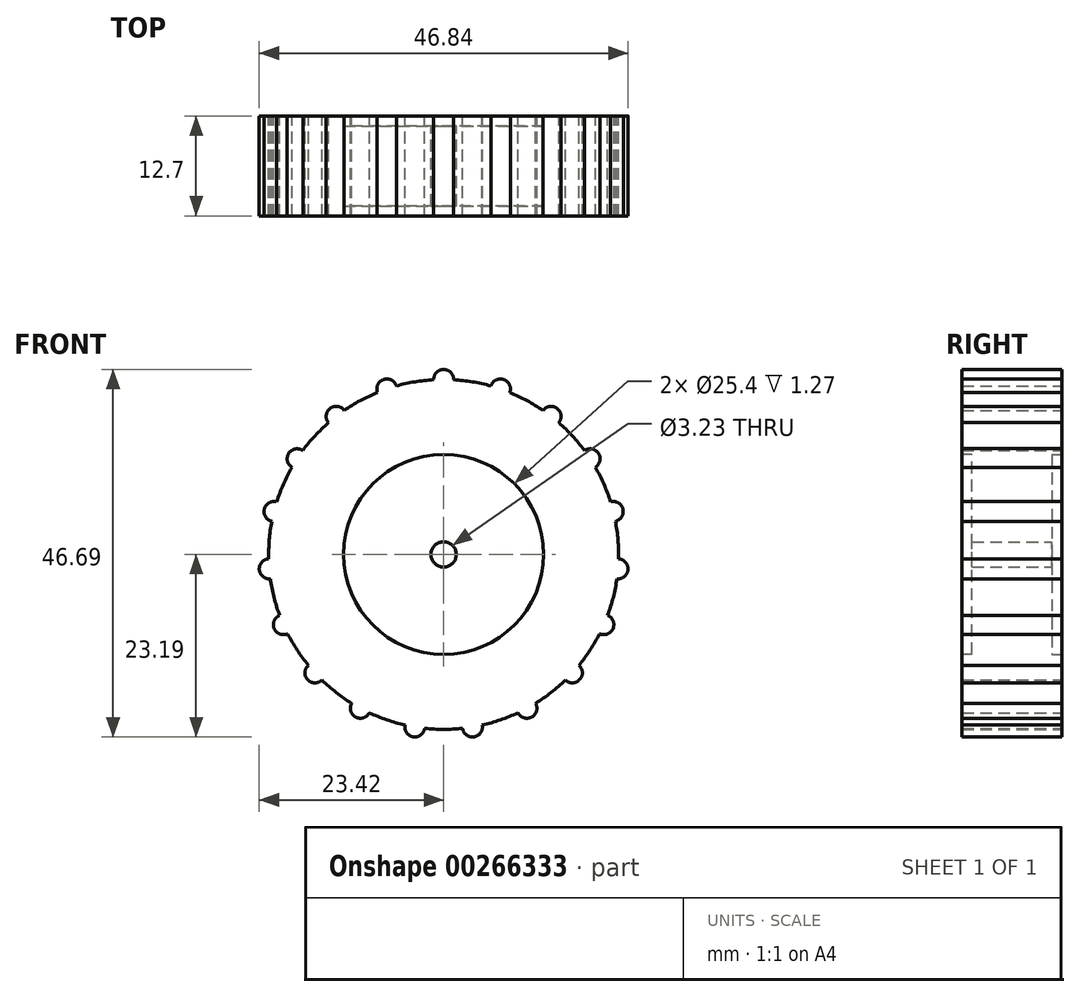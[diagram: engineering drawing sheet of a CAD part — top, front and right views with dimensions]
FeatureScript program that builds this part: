
annotation { "Feature Type Name" : "Feature", "Feature Type Description" : "" }
export const myFeature = defineFeature(function(context is Context, id is Id, definition is map)
    precondition{}
    {
        {
            var Q0;
            Q0=qCreatedBy(makeId("Front.planeOp"),FACE);
            var sketch = newSketch(context, id + "F0", { "sketchPlane" : qUnion([Q0])});
            skCircle(sketch, "E0", {"center": v(0, 0) * mm, "radius": 16.51 * mm});
            skArc(sketch, "E1", {"start": v(-1.27, 22.19) * mm, "mid": v(-3.66, 21.92) * mm, "end": v(-6, 21.4) * mm});
            skCircle(sketch, "E2", {"center": v(0, 0) * mm, "radius": 1.61 * mm});
            skArc(sketch, "E3", {"start": v(1.27, 22.19) * mm, "mid": v(0, 23.5) * mm, "end": v(-1.27, 22.19) * mm});
            skArc(sketch, "E4.1.0", {"start": v(8.4, 20.57) * mm, "mid": v(7.63, 22.22) * mm, "end": v(6, 21.4) * mm});
            skArc(sketch, "E4.2.0", {"start": v(14.63, 16.73) * mm, "mid": v(14.43, 18.54) * mm, "end": v(12.63, 18.29) * mm});
            skArc(sketch, "E4.3.0", {"start": v(19.27, 11.07) * mm, "mid": v(19.67, 12.85) * mm, "end": v(17.88, 13.2) * mm});
            skArc(sketch, "E4.4.0", {"start": v(21.82, 4.22) * mm, "mid": v(22.78, 5.77) * mm, "end": v(21.2, 6.68) * mm});
            skArc(sketch, "E4.5.0", {"start": v(22, -3.1) * mm, "mid": v(23.41, -1.94) * mm, "end": v(22.22, -0.57) * mm});
            skArc(sketch, "E4.6.0", {"start": v(19.8, -10.08) * mm, "mid": v(21.52, -9.44) * mm, "end": v(20.83, -7.75) * mm});
            skArc(sketch, "E4.7.0", {"start": v(15.46, -15.96) * mm, "mid": v(17.29, -15.91) * mm, "end": v(17.18, -14.1) * mm});
            skArc(sketch, "E4.8.0", {"start": v(9.44, -20.12) * mm, "mid": v(11.18, -20.66) * mm, "end": v(11.68, -18.91) * mm});
            skArc(sketch, "E4.9.0", {"start": v(2.4, -22.1) * mm, "mid": v(3.87, -23.17) * mm, "end": v(4.9, -21.68) * mm});
            skArc(sketch, "E4.10.0", {"start": v(-4.9, -21.68) * mm, "mid": v(-3.87, -23.17) * mm, "end": v(-2.4, -22.1) * mm});
            skArc(sketch, "E4.11.0", {"start": v(-11.68, -18.91) * mm, "mid": v(-11.18, -20.66) * mm, "end": v(-9.44, -20.12) * mm});
            skArc(sketch, "E4.12.0", {"start": v(-17.18, -14.1) * mm, "mid": v(-17.29, -15.91) * mm, "end": v(-15.46, -15.96) * mm});
            skArc(sketch, "E4.13.0", {"start": v(-20.83, -7.75) * mm, "mid": v(-21.52, -9.44) * mm, "end": v(-19.8, -10.08) * mm});
            skArc(sketch, "E4.14.0", {"start": v(-22.22, -0.57) * mm, "mid": v(-23.41, -1.94) * mm, "end": v(-22, -3.1) * mm});
            skArc(sketch, "E4.15.0", {"start": v(-21.2, 6.68) * mm, "mid": v(-22.78, 5.77) * mm, "end": v(-21.82, 4.22) * mm});
            skArc(sketch, "E4.16.0", {"start": v(-17.88, 13.2) * mm, "mid": v(-19.67, 12.85) * mm, "end": v(-19.27, 11.07) * mm});
            skArc(sketch, "E4.17.0", {"start": v(-12.63, 18.29) * mm, "mid": v(-14.43, 18.54) * mm, "end": v(-14.63, 16.73) * mm});
            skArc(sketch, "E4.18.0", {"start": v(-6, 21.4) * mm, "mid": v(-7.63, 22.22) * mm, "end": v(-8.4, 20.57) * mm});
            skLineSegment(sketch, "E4.anchor1", {"start": v(0, 0) * mm, "end": v(-1.27, 22.19) * mm, "construction": true});
            skLineSegment(sketch, "E4.anchor2", {"start": v(0, 0) * mm, "end": v(-1.27, 22.19) * mm, "construction": true});
            skPoint(sketch, "E5.endSnap0", {"position": v(0, 23.5) * mm});
            skArc(sketch, "E6.trimOffspring", {"start": v(-8.4, 20.57) * mm, "mid": v(0.63, -22.22) * mm, "end": v(7.22, 21.02) * mm});
            skArc(sketch, "E7.trimOffspring", {"start": v(6, 21.4) * mm, "mid": v(3.66, 21.92) * mm, "end": v(1.27, 22.19) * mm});
            skSolve(sketch);
        }
        {
            var Q0;
            Q0=makeQuery(id+"F0.imprint","IMPRINT",FACE,{"disambiguationData":[TD([[makeQuery(id+"F0.imprint","IMPRINT",EDGE,{"derivedFrom":sQuery(id+"F0.wireOp",EDGE,"E0")}),1.0]])]});
            var Q1;
            Q1=makeQuery(id+"F0.imprint","IMPRINT",FACE,{"disambiguationData":[TD([[makeQuery(id+"F0.imprint","IMPRINT",EDGE,{"derivedFrom":sQuery(id+"F0.wireOp",EDGE,"E1")}),1.0]])]});
            var Q2;
            {var subQ0=sQuery(id+"F0.wireOp",EDGE,"E4.16.0");Q2=makeQuery(id+"F0.imprint","IMPRINT",FACE,{"disambiguationData":[TD([[makeQuery(id+"F0.imprint","IMPRINT",EDGE,{"derivedFrom":subQ0}),1.0]])]});}
            var Q3;
            {var subQ0=sQuery(id+"F0.wireOp",EDGE,"E4.17.0");Q3=makeQuery(id+"F0.imprint","IMPRINT",FACE,{"disambiguationData":[TD([[makeQuery(id+"F0.imprint","IMPRINT",EDGE,{"derivedFrom":subQ0}),1.0]])]});}
            var Q4;
            {var subQ0=sQuery(id+"F0.wireOp",EDGE,"E4.2.0");Q4=makeQuery(id+"F0.imprint","IMPRINT",FACE,{"disambiguationData":[TD([[makeQuery(id+"F0.imprint","IMPRINT",EDGE,{"derivedFrom":subQ0}),1.0]])]});}
            var Q5;
            {var subQ0=sQuery(id+"F0.wireOp",EDGE,"E4.3.0");Q5=makeQuery(id+"F0.imprint","IMPRINT",FACE,{"disambiguationData":[TD([[makeQuery(id+"F0.imprint","IMPRINT",EDGE,{"derivedFrom":subQ0}),1.0]])]});}
            var Q6;
            {var subQ0=sQuery(id+"F0.wireOp",EDGE,"E4.4.0");Q6=makeQuery(id+"F0.imprint","IMPRINT",FACE,{"disambiguationData":[TD([[makeQuery(id+"F0.imprint","IMPRINT",EDGE,{"derivedFrom":subQ0}),1.0]])]});}
            var Q7;
            {var subQ0=sQuery(id+"F0.wireOp",EDGE,"E4.5.0");Q7=makeQuery(id+"F0.imprint","IMPRINT",FACE,{"disambiguationData":[TD([[makeQuery(id+"F0.imprint","IMPRINT",EDGE,{"derivedFrom":subQ0}),1.0]])]});}
            var Q8;
            {var subQ0=sQuery(id+"F0.wireOp",EDGE,"E4.15.0");Q8=makeQuery(id+"F0.imprint","IMPRINT",FACE,{"disambiguationData":[TD([[makeQuery(id+"F0.imprint","IMPRINT",EDGE,{"derivedFrom":subQ0}),1.0]])]});}
            var Q9;
            {var subQ0=sQuery(id+"F0.wireOp",EDGE,"E4.14.0");Q9=makeQuery(id+"F0.imprint","IMPRINT",FACE,{"disambiguationData":[TD([[makeQuery(id+"F0.imprint","IMPRINT",EDGE,{"derivedFrom":subQ0}),1.0]])]});}
            var Q10;
            {var subQ0=sQuery(id+"F0.wireOp",EDGE,"E4.13.0");Q10=makeQuery(id+"F0.imprint","IMPRINT",FACE,{"disambiguationData":[TD([[makeQuery(id+"F0.imprint","IMPRINT",EDGE,{"derivedFrom":subQ0}),1.0]])]});}
            var Q11;
            {var subQ0=sQuery(id+"F0.wireOp",EDGE,"E4.12.0");Q11=makeQuery(id+"F0.imprint","IMPRINT",FACE,{"disambiguationData":[TD([[makeQuery(id+"F0.imprint","IMPRINT",EDGE,{"derivedFrom":subQ0}),1.0]])]});}
            var Q12;
            {var subQ0=sQuery(id+"F0.wireOp",EDGE,"E4.11.0");Q12=makeQuery(id+"F0.imprint","IMPRINT",FACE,{"disambiguationData":[TD([[makeQuery(id+"F0.imprint","IMPRINT",EDGE,{"derivedFrom":subQ0}),1.0]])]});}
            var Q13;
            {var subQ0=sQuery(id+"F0.wireOp",EDGE,"E4.10.0");Q13=makeQuery(id+"F0.imprint","IMPRINT",FACE,{"disambiguationData":[TD([[makeQuery(id+"F0.imprint","IMPRINT",EDGE,{"derivedFrom":subQ0}),1.0]])]});}
            var Q14;
            {var subQ0=sQuery(id+"F0.wireOp",EDGE,"E4.9.0");Q14=makeQuery(id+"F0.imprint","IMPRINT",FACE,{"disambiguationData":[TD([[makeQuery(id+"F0.imprint","IMPRINT",EDGE,{"derivedFrom":subQ0}),1.0]])]});}
            var Q15;
            {var subQ0=sQuery(id+"F0.wireOp",EDGE,"E4.8.0");Q15=makeQuery(id+"F0.imprint","IMPRINT",FACE,{"disambiguationData":[TD([[makeQuery(id+"F0.imprint","IMPRINT",EDGE,{"derivedFrom":subQ0}),1.0]])]});}
            var Q16;
            {var subQ0=sQuery(id+"F0.wireOp",EDGE,"E4.7.0");Q16=makeQuery(id+"F0.imprint","IMPRINT",FACE,{"disambiguationData":[TD([[makeQuery(id+"F0.imprint","IMPRINT",EDGE,{"derivedFrom":subQ0}),1.0]])]});}
            var Q17;
            {var subQ0=sQuery(id+"F0.wireOp",EDGE,"E4.6.0");Q17=makeQuery(id+"F0.imprint","IMPRINT",FACE,{"disambiguationData":[TD([[makeQuery(id+"F0.imprint","IMPRINT",EDGE,{"derivedFrom":subQ0}),1.0]])]});}
            extrude(context, id + "F1", {"entities" : qUnion([Q0, Q1, Q2, Q3, Q4, Q5, Q6, Q7, Q8, Q9, Q10, Q11, Q12, Q13, Q14, Q15, Q16, Q17]), "depth" : 12.7 * mm});
        }
        {
            var Q0;
            Q0=makeQuery(id+"F1.opExtrude","CAP_FACE",FACE,{"disambiguationData":[OSD([sQuery(id+"F0.wireOp",EDGE,"E1"),sQuery(id+"F0.wireOp",EDGE,"E2")])],"isStart":false});
            var sketch = newSketch(context, id + "F2", { "sketchPlane" : qUnion([Q0])});
            skCircle(sketch, "E8", {"center": v(0, 0) * mm, "radius": 12.7 * mm});
            skSolve(sketch);
        }
        {
            var Q0;
            Q0=makeQuery(id+"F1.opExtrude","CAP_FACE",FACE,{"disambiguationData":[OSD([sQuery(id+"F0.wireOp",EDGE,"E1"),sQuery(id+"F0.wireOp",EDGE,"E2")])],"isStart":true});
            var sketch = newSketch(context, id + "F3", { "sketchPlane" : qUnion([Q0])});
            skCircle(sketch, "E9", {"center": v(0, 0) * mm, "radius": 12.7 * mm});
            skSolve(sketch);
        }
        {
            var Q0;
            Q0=makeQuery(id+"F3.imprint","IMPRINT",FACE,{"disambiguationData":[TD([[makeQuery(id+"F3.imprint","IMPRINT",EDGE,{"derivedFrom":sQuery(id+"F3.wireOp",EDGE,"E9")}),1.0]])]});
            var Q1;
            Q1=makeQuery(id+"F2.imprint","IMPRINT",FACE,{"disambiguationData":[TD([[makeQuery(id+"F2.imprint","IMPRINT",EDGE,{"derivedFrom":sQuery(id+"F2.wireOp",EDGE,"E8")}),1.0]])]});
            extrude(context, id + "F4", {"entities" : qUnion([Q0, Q1]), "operationType" : NewBodyOperationType.REMOVE, "oppositeDirection" : true, "depth" : 1.27 * mm});
        }
        {
            var Q0;
            Q0 = qSketchRegion(id + "F2", true);
            extrude(context, id + "F5", {"entities" : qUnion([Q0]), "operationType" : NewBodyOperationType.REMOVE, "oppositeDirection" : true, "depth" : 1.27 * mm});
        }
        {
            var Q0;
            Q0=makeQuery(id+"F2.imprint","IMPRINT",FACE,{"disambiguationData":[TD([[makeQuery(id+"F2.imprint","IMPRINT",EDGE,{"derivedFrom":sQuery(id+"F2.wireOp",EDGE,"E8")}),1.0]])]});
            var sketch = newSketch(context, id + "F6", { "sketchPlane" : qUnion([Q0])});
            skText(sketch, "E10", { "text": "Jason", "fontName": "OpenSans-Regular.ttf"});
            const initialGuessF6  = {"E10": [-0.008, 0.0036, 1, 0, 0.00437]};
            skSetInitialGuess(sketch, initialGuessF6);
            skSolve(sketch);
        }
        {
            var Q0;
            Q0 = qSketchRegion(id + "F6", true);
            var Q1;
            Q1 = qConstructionFilter(qBodyType(qCreatedBy(id + "F6" ,EDGE), BodyType.WIRE), ConstructionObject.NO);
            extrude(context, id + "F7", {"entities" : qUnion([Q0]), "bodyType" : ToolBodyType.SURFACE, "operationType" : NewBodyOperationType.ADD, "surfaceEntities" : qUnion([Q1]), "oppositeDirection" : true, "depth" : 0.25 * mm});
        }
    });
